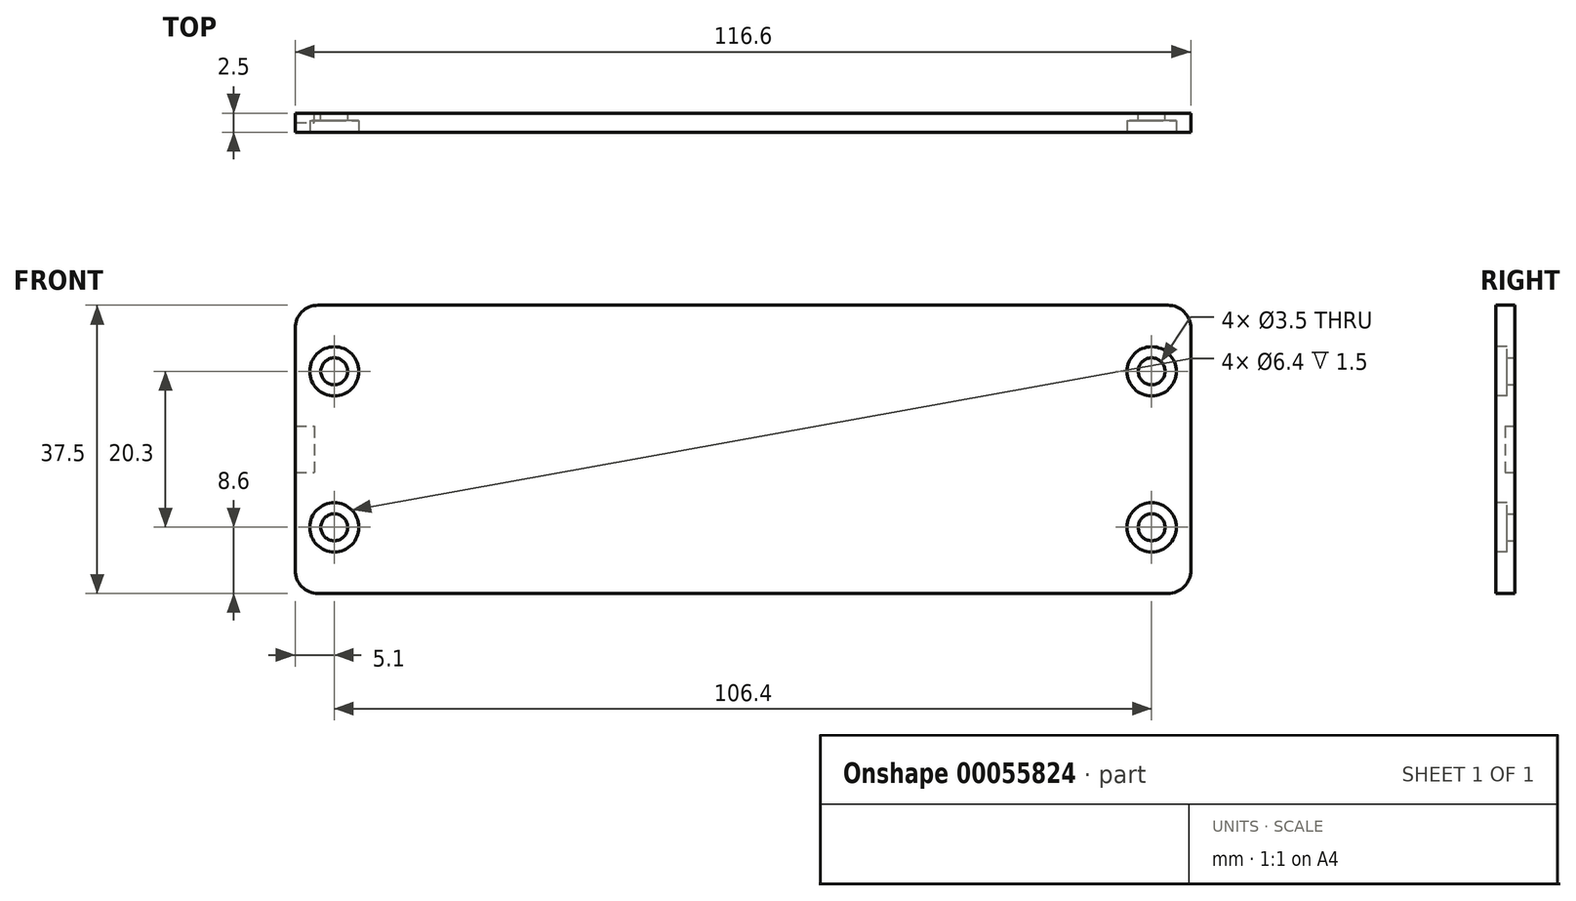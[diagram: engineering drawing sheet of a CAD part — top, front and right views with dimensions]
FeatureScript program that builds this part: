
annotation { "Feature Type Name" : "Feature", "Feature Type Description" : "" }
export const myFeature = defineFeature(function(context is Context, id is Id, definition is map)
    precondition{}
    {
        {
            var Q0;
            Q0=qCreatedBy(makeId("Front.planeOp"),FACE);
            var sketch = newSketch(context, id + "F0", { "sketchPlane" : qUnion([Q0])});
            skLineSegment(sketch, "E0.bottom", {"start": v(-55.3, 18.75) * mm, "end": v(55.3, 18.75) * mm});
            skLineSegment(sketch, "E0.top", {"start": v(-55.3, -18.75) * mm, "end": v(55.3, -18.75) * mm});
            skLineSegment(sketch, "E0.left", {"start": v(-58.3, 15.75) * mm, "end": v(-58.3, -15.75) * mm});
            skLineSegment(sketch, "E0.right", {"start": v(58.3, 15.75) * mm, "end": v(58.3, -15.75) * mm});
            skPoint(sketch, "E1.visualSharp", {"position": v(-58.3, 18.75) * mm});
            skArc(sketch, "E1.filletArc", {"start": v(-55.3, 18.75) * mm, "mid": v(-57.42, 17.87) * mm, "end": v(-58.3, 15.75) * mm});
            skPoint(sketch, "E2.visualSharp", {"position": v(58.3, 18.75) * mm});
            skArc(sketch, "E2.filletArc", {"start": v(58.3, 15.75) * mm, "mid": v(57.42, 17.87) * mm, "end": v(55.3, 18.75) * mm});
            skPoint(sketch, "E3.visualSharp", {"position": v(58.3, -18.75) * mm});
            skArc(sketch, "E3.filletArc", {"start": v(55.3, -18.75) * mm, "mid": v(57.42, -17.87) * mm, "end": v(58.3, -15.75) * mm});
            skPoint(sketch, "E4.visualSharp", {"position": v(-58.3, -18.75) * mm});
            skArc(sketch, "E4.filletArc", {"start": v(-58.3, -15.75) * mm, "mid": v(-57.42, -17.87) * mm, "end": v(-55.3, -18.75) * mm});
            skCircle(sketch, "E5", {"center": v(-53.2, 10.15) * mm, "radius": 1.75 * mm});
            skCircle(sketch, "E6", {"center": v(53.2, 10.15) * mm, "radius": 1.75 * mm});
            skCircle(sketch, "E7", {"center": v(-53.2, -10.15) * mm, "radius": 1.75 * mm});
            skCircle(sketch, "E8", {"center": v(53.2, -10.15) * mm, "radius": 1.75 * mm});
            skSolve(sketch);
        }
        {
            var Q0;
            Q0=makeQuery(id+"F0.imprint","IMPRINT",FACE,{"disambiguationData":[TD([[makeQuery(id+"F0.imprint","IMPRINT",EDGE,{"derivedFrom":sQuery(id+"F0.wireOp",EDGE,"E0.bottom")}),-1.0]])]});
            extrude(context, id + "F1", {"entities" : qUnion([Q0]), "depth" : 2.5 * mm});
        }
        {
            var Q0;
            Q0=makeQuery(id+"F1.opExtrude","CAP_FACE",FACE,{"disambiguationData":[OSD([sQuery(id+"F0.wireOp",EDGE,"E0.bottom"),sQuery(id+"F0.wireOp",EDGE,"E0.top"),sQuery(id+"F0.wireOp",EDGE,"E0.left"),sQuery(id+"F0.wireOp",EDGE,"E0.right"),sQuery(id+"F0.wireOp",EDGE,"E1.filletArc"),sQuery(id+"F0.wireOp",EDGE,"E2.filletArc"),sQuery(id+"F0.wireOp",EDGE,"E3.filletArc"),sQuery(id+"F0.wireOp",EDGE,"E4.filletArc"),sQuery(id+"F0.wireOp",EDGE,"E5"),sQuery(id+"F0.wireOp",EDGE,"E6"),sQuery(id+"F0.wireOp",EDGE,"E7"),sQuery(id+"F0.wireOp",EDGE,"E8")])],"isStart":false});
            var sketch = newSketch(context, id + "F2", { "sketchPlane" : qUnion([Q0])});
            skCircle(sketch, "E9", {"center": v(-53.2, 10.15) * mm, "radius": 3.2 * mm});
            skCircle(sketch, "E10", {"center": v(53.2, 10.15) * mm, "radius": 3.2 * mm});
            skCircle(sketch, "E11", {"center": v(-53.2, -10.15) * mm, "radius": 3.2 * mm});
            skCircle(sketch, "E12", {"center": v(53.2, -10.15) * mm, "radius": 3.2 * mm});
            skSolve(sketch);
        }
        {
            var Q0;
            Q0=qSketchRegion(id+"F2",true);
            extrude(context, id + "F3", {"entities" : qUnion([Q0]), "operationType" : NewBodyOperationType.REMOVE, "oppositeDirection" : true, "depth" : 1.5 * mm});
        }
        {
            var Q0;
            Q0=makeQuery(id+"F1.opExtrude","CAP_FACE",FACE,{"disambiguationData":[OSD([sQuery(id+"F0.wireOp",EDGE,"E0.bottom"),sQuery(id+"F0.wireOp",EDGE,"E0.top"),sQuery(id+"F0.wireOp",EDGE,"E0.left"),sQuery(id+"F0.wireOp",EDGE,"E0.right"),sQuery(id+"F0.wireOp",EDGE,"E1.filletArc"),sQuery(id+"F0.wireOp",EDGE,"E2.filletArc"),sQuery(id+"F0.wireOp",EDGE,"E3.filletArc"),sQuery(id+"F0.wireOp",EDGE,"E4.filletArc"),sQuery(id+"F0.wireOp",EDGE,"E5"),sQuery(id+"F0.wireOp",EDGE,"E6"),sQuery(id+"F0.wireOp",EDGE,"E7"),sQuery(id+"F0.wireOp",EDGE,"E8")])],"isStart":true});
            var sketch = newSketch(context, id + "F4", { "sketchPlane" : qUnion([Q0])});
            skLineSegment(sketch, "E13.bottom", {"start": v(58.3, 3) * mm, "end": v(55.8, 3) * mm});
            skLineSegment(sketch, "E13.top", {"start": v(58.3, -3) * mm, "end": v(55.8, -3) * mm});
            skLineSegment(sketch, "E13.left", {"start": v(58.3, 3) * mm, "end": v(58.3, -3) * mm});
            skLineSegment(sketch, "E13.right", {"start": v(55.8, 3) * mm, "end": v(55.8, -3) * mm});
            skSolve(sketch);
        }
        {
            var Q0;
            Q0=qSketchRegion(id+"F4",true);
            extrude(context, id + "F5", {"entities" : qUnion([Q0]), "operationType" : NewBodyOperationType.REMOVE, "oppositeDirection" : true, "depth" : 1.25 * mm});
        }
    });
